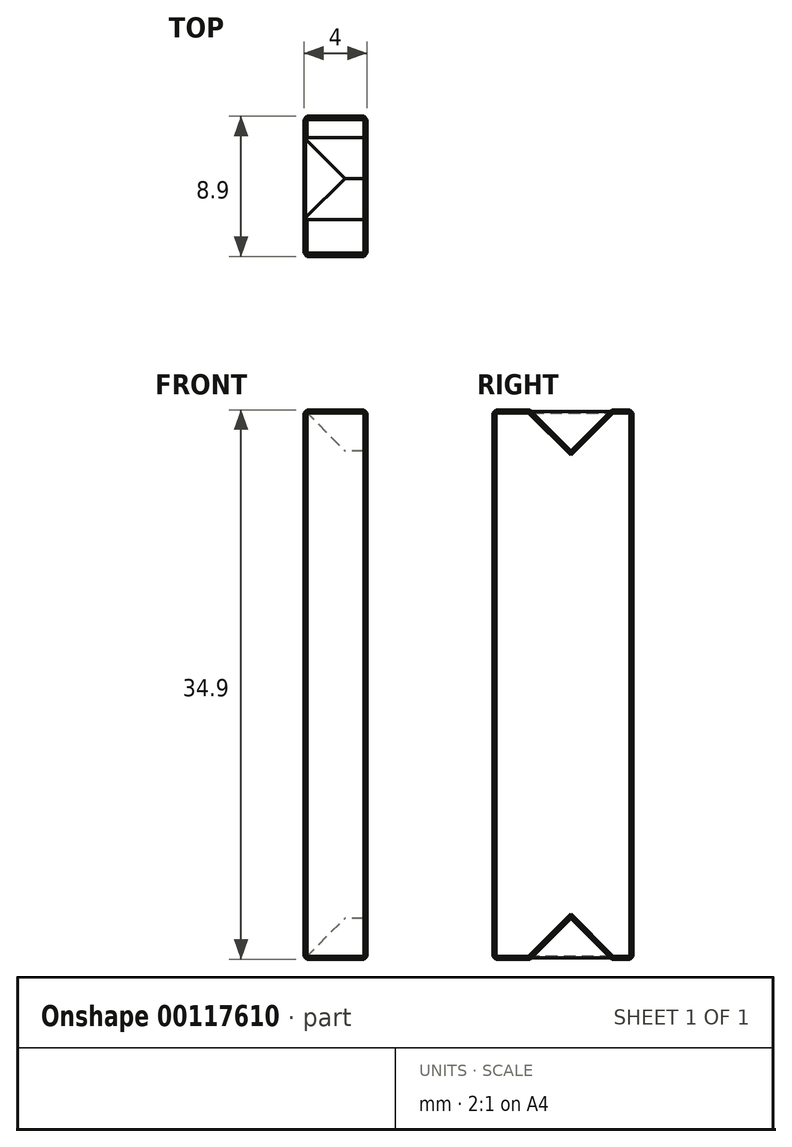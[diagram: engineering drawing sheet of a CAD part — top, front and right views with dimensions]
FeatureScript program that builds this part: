
annotation { "Feature Type Name" : "Feature", "Feature Type Description" : "" }
export const myFeature = defineFeature(function(context is Context, id is Id, definition is map)
    precondition{}
    {
        {
            var Q0;
            Q0=qCreatedBy(makeId("Right.planeOp"),FACE);
            var sketch = newSketch(context, id + "F0", { "sketchPlane" : qUnion([Q0])});
            skLineSegment(sketch, "E0.bottom", {"start": v(4.45, 17.45) * mm, "end": v(3.1, 17.45) * mm});
            skLineSegment(sketch, "E0.top", {"start": v(4.45, -17.45) * mm, "end": v(3.1, -17.45) * mm});
            skLineSegment(sketch, "E0.left", {"start": v(4.45, 17.45) * mm, "end": v(4.45, -17.45) * mm});
            skLineSegment(sketch, "E0.right", {"start": v(-4.45, 17.45) * mm, "end": v(-4.45, -17.45) * mm});
            skPoint(sketch, "E0.middle", {"position": v(0, 0) * mm});
            skLineSegment(sketch, "E1", {"start": v(0.5, 17.45) * mm, "end": v(0.5, -17.45) * mm, "construction": true});
            skLineSegment(sketch, "E2", {"start": v(0.5, 0) * mm, "end": v(-4.45, 0) * mm, "construction": true});
            skLineSegment(sketch, "E3", {"start": v(3.1, 17.45) * mm, "end": v(0.5, 14.85) * mm});
            skLineSegment(sketch, "E4", {"start": v(0.5, 14.85) * mm, "end": v(-2.1, 17.45) * mm});
            skLineSegment(sketch, "E5.MirrorCS", {"start": v(3.1, -17.45) * mm, "end": v(0.5, -14.85) * mm});
            skLineSegment(sketch, "E6.MirrorCS", {"start": v(0.5, -14.85) * mm, "end": v(-2.1, -17.45) * mm});
            skLineSegment(sketch, "E7.trimOffspring", {"start": v(-2.1, 17.45) * mm, "end": v(-4.45, 17.45) * mm});
            skLineSegment(sketch, "E8.trimOffspring", {"start": v(-2.1, -17.45) * mm, "end": v(-4.45, -17.45) * mm});
            skSolve(sketch);
        }
        {
            var Q0;
            Q0 = qSketchRegion(id + "F0", true);
            extrude(context, id + "F1", {"entities" : qUnion([Q0]), "depth" : 4 * mm});
        }
        {
            var Q0;
            Q0=makeQuery(id+"F1.opExtrude","SWEPT_FACE",FACE,{"disambiguationData":[OSD([sQuery(id+"F0.wireOp",EDGE,"E0.right")])]});
            var sketch = newSketch(context, id + "F2", { "sketchPlane" : qUnion([Q0])});
            skLineSegment(sketch, "E9", {"start": v(0, 17.45) * mm, "end": v(0, 14.85) * mm});
            skLineSegment(sketch, "E10", {"start": v(0, 14.85) * mm, "end": v(2.6, 14.85) * mm});
            skLineSegment(sketch, "E11", {"start": v(2.6, 14.85) * mm, "end": v(0, 17.45) * mm});
            skLineSegment(sketch, "E12", {"start": v(0, 0) * mm, "end": v(4, 0) * mm, "construction": true});
            skLineSegment(sketch, "E13.MirrorCS", {"start": v(0, -14.85) * mm, "end": v(2.6, -14.85) * mm});
            skLineSegment(sketch, "E14.MirrorCS", {"start": v(2.6, -14.85) * mm, "end": v(0, -17.45) * mm});
            skLineSegment(sketch, "E15.MirrorCS", {"start": v(0, -17.45) * mm, "end": v(0, -14.85) * mm});
            skSolve(sketch);
        }
        {
            var Q0;
            Q0 = qSketchRegion(id + "F2", true);
            var Q1;
            Q1=makeQuery(id+"F1.opExtrude","SWEPT_FACE",FACE,{"disambiguationData":[OSD([sQuery(id+"F0.wireOp",EDGE,"E0.left")])]});
            extrude(context, id + "F3", {"entities" : qUnion([Q0]), "operationType" : NewBodyOperationType.ADD, "endBound" : BoundingType.UP_TO_SURFACE, "oppositeDirection" : true, "endBoundEntityFace" : qUnion([Q1]), "depth" : 25 * mm});
        }
        {
            var Q0;
            Q0=makeQuery(id+"F1.opExtrude","CAP_EDGE",EDGE,{"disambiguationData":[OSD([sQuery(id+"F0.wireOp",EDGE,"E0.right")])],"isStart":true});
            var Q1;
            Q1=makeQuery(id+"F1.opExtrude","CAP_EDGE",EDGE,{"disambiguationData":[OSD([sQuery(id+"F0.wireOp",EDGE,"E7.trimOffspring")])],"isStart":true});
            var Q2;
            Q2=makeQuery(id+"F1.opExtrude","CAP_EDGE",EDGE,{"disambiguationData":[OSD([sQuery(id+"F0.wireOp",EDGE,"E0.left")])],"isStart":true});
            var Q3;
            Q3=makeQuery(id+"F1.opExtrude","SWEPT_EDGE",EDGE,{"disambiguationData":[OSD([sQuery(id+"F0.wireOp",EDGE,"E0.bottom"),sQuery(id+"F0.wireOp",EDGE,"E0.left")])]});
            var Q4;
            Q4=makeQuery(id+"F1.opExtrude","SWEPT_EDGE",EDGE,{"disambiguationData":[OSD([sQuery(id+"F0.wireOp",EDGE,"E0.right"),sQuery(id+"F0.wireOp",EDGE,"E7.trimOffspring")])]});
            var Q5;
            Q5=makeQuery(id+"F1.opExtrude","SWEPT_EDGE",EDGE,{"disambiguationData":[OSD([sQuery(id+"F0.wireOp",EDGE,"E0.right"),sQuery(id+"F0.wireOp",EDGE,"E8.trimOffspring")])]});
            var Q6;
            Q6=makeQuery(id+"F1.opExtrude","CAP_EDGE",EDGE,{"disambiguationData":[OSD([sQuery(id+"F0.wireOp",EDGE,"E8.trimOffspring")])],"isStart":true});
            var Q7;
            Q7=makeQuery(id+"F1.opExtrude","SWEPT_EDGE",EDGE,{"disambiguationData":[OSD([sQuery(id+"F0.wireOp",EDGE,"E0.top"),sQuery(id+"F0.wireOp",EDGE,"E0.left")])]});
            var Q8;
            Q8=makeQuery(id+"F1.opExtrude","CAP_EDGE",EDGE,{"disambiguationData":[OSD([sQuery(id+"F0.wireOp",EDGE,"E5.MirrorCS")])],"isStart":false});
            var Q9;
            Q9=makeQuery(id+"F1.opExtrude","CAP_EDGE",EDGE,{"disambiguationData":[OSD([sQuery(id+"F0.wireOp",EDGE,"E6.MirrorCS")])],"isStart":false});
            var Q10;
            Q10=makeQuery(id+"F1.opExtrude","CAP_EDGE",EDGE,{"disambiguationData":[OSD([sQuery(id+"F0.wireOp",EDGE,"E8.trimOffspring")])],"isStart":false});
            var Q11;
            Q11=makeQuery(id+"F1.opExtrude","CAP_EDGE",EDGE,{"disambiguationData":[OSD([sQuery(id+"F0.wireOp",EDGE,"E0.right")])],"isStart":false});
            var Q12;
            Q12=makeQuery(id+"F1.opExtrude","CAP_EDGE",EDGE,{"disambiguationData":[OSD([sQuery(id+"F0.wireOp",EDGE,"E0.top")])],"isStart":false});
            var Q13;
            Q13=makeQuery(id+"F1.opExtrude","CAP_EDGE",EDGE,{"disambiguationData":[OSD([sQuery(id+"F0.wireOp",EDGE,"E0.left")])],"isStart":false});
            var Q14;
            Q14=makeQuery(id+"F1.opExtrude","CAP_EDGE",EDGE,{"disambiguationData":[OSD([sQuery(id+"F0.wireOp",EDGE,"E3")])],"isStart":false});
            var Q15;
            Q15=makeQuery(id+"F1.opExtrude","CAP_EDGE",EDGE,{"disambiguationData":[OSD([sQuery(id+"F0.wireOp",EDGE,"E4")])],"isStart":false});
            var Q16;
            Q16=makeQuery(id+"F1.opExtrude","CAP_EDGE",EDGE,{"disambiguationData":[OSD([sQuery(id+"F0.wireOp",EDGE,"E7.trimOffspring")])],"isStart":false});
            var Q17;
            Q17=makeQuery(id+"F1.opExtrude","CAP_EDGE",EDGE,{"disambiguationData":[OSD([sQuery(id+"F0.wireOp",EDGE,"E0.bottom")])],"isStart":false});
            chamfer(context, id + "F4", {"entities" : qUnion([Q0, Q1, Q2, Q3, Q4, Q5, Q6, Q7, Q8, Q9, Q10, Q11, Q12, Q13, Q14, Q15, Q16, Q17]), "width" : .2 * mm, "tangentPropagation" : true});
        }
    });
